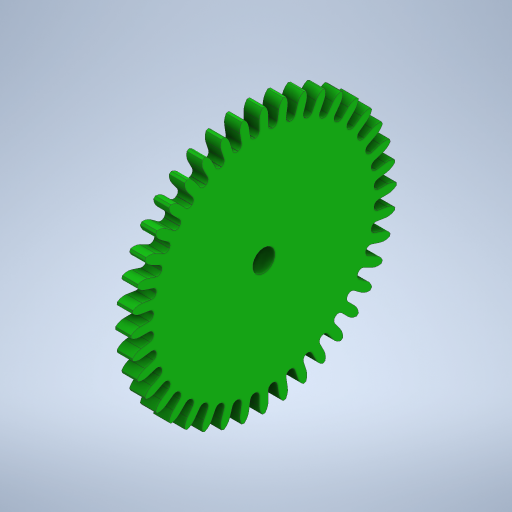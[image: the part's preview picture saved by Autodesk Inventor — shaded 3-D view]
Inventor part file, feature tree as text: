
AUTODESK INVENTOR PART (.ipt)
format: ipt  version: 2024 (Build 280153020, 153B)  size: 896,000 bytes
history: native  units: mm
features: extrude x1, sketch x1
ambient origin geometry x8: Origin, YZ Plane, XZ Plane, XY Plane, X Axis, Y Axis, Z Axis, Center Point
bodies: Body1 (feature_tree)
feature tree (2):
  extrude  "Extrusion2"  Depth=3.5mm
  sketch  "Sketch1"  dims[d0=5.0mm d1=50.0mm d2=3.0mm d3=2.0mm d4=1.570796mm d5=0.785398mm d7=2.04mm d8=1.02mm d9=0.3mm d10=0.6mm d11=3.0mm d12=3.0mm d13=1.0mm d14=400.0mm d16=360.0deg d20=3.5mm d21=0.0mm]
